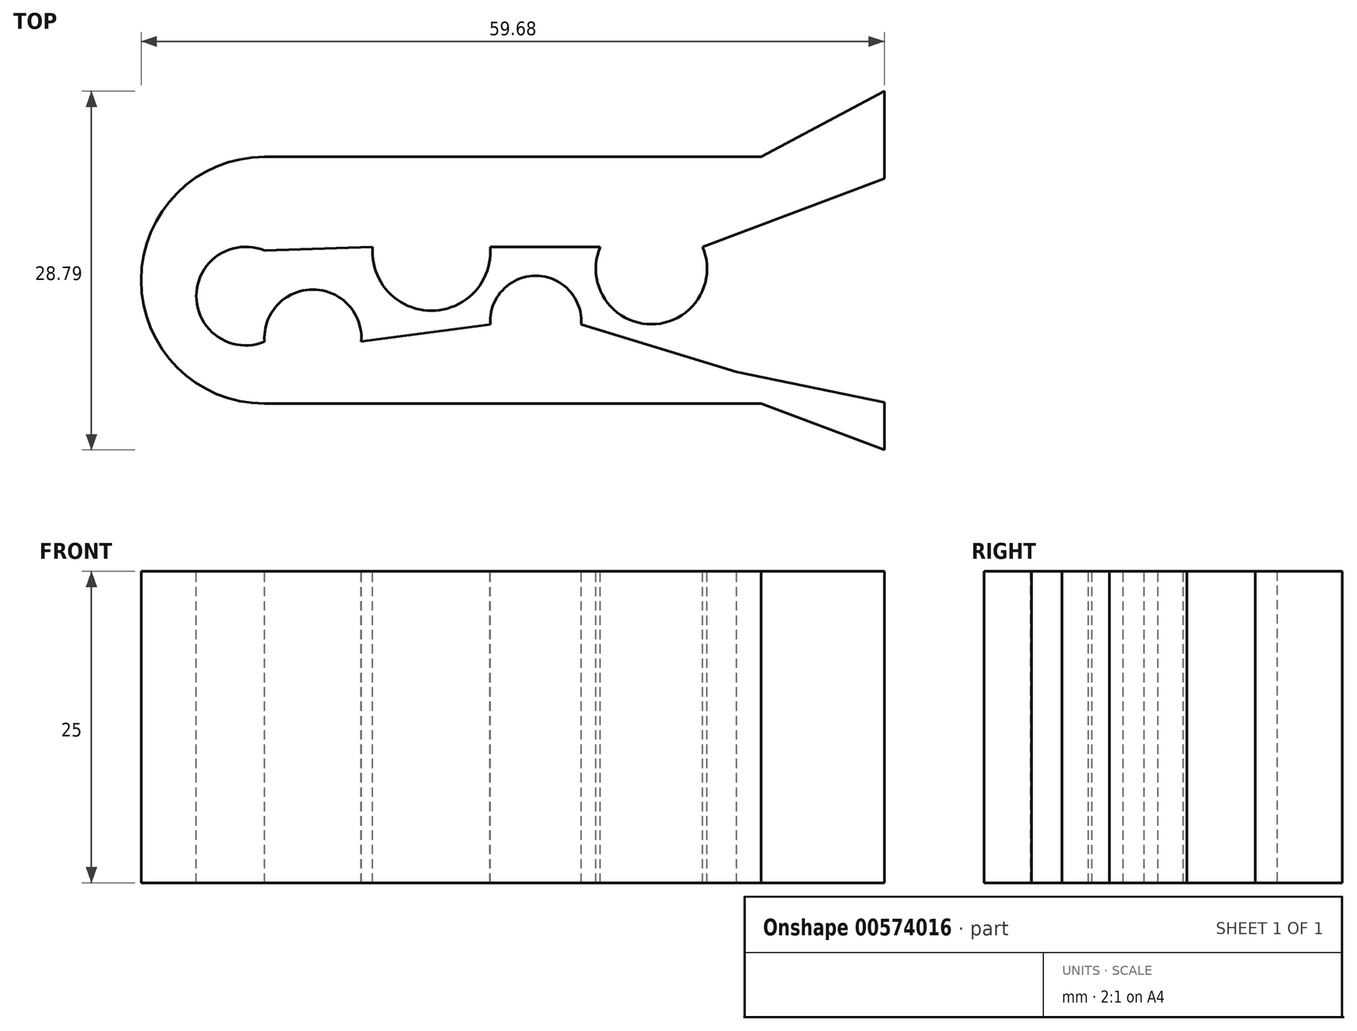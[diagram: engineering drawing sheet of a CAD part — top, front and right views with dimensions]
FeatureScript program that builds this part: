
annotation { "Feature Type Name" : "Feature", "Feature Type Description" : "" }
export const myFeature = defineFeature(function(context is Context, id is Id, definition is map)
    precondition{}
    {
        {
            var Q0;
            Q0=qCreatedBy(makeId("Top.planeOp"),FACE);
            var sketch = newSketch(context, id + "F0", { "sketchPlane" : qUnion([Q0])});
            skLineSegment(sketch, "E0", {"start": v(0, -45.03) * mm, "end": v(39.88, -45.03) * mm});
            skLineSegment(sketch, "E1", {"start": v(39.88, -45.03) * mm, "end": v(49.78, -48.75) * mm});
            skLineSegment(sketch, "E2", {"start": v(49.78, -48.75) * mm, "end": v(49.78, -19.96) * mm});
            skLineSegment(sketch, "E3", {"start": v(49.78, -19.96) * mm, "end": v(39.88, -25.23) * mm});
            skLineSegment(sketch, "E4", {"start": v(39.88, -25.23) * mm, "end": v(0, -25.23) * mm});
            skArc(sketch, "E5", {"start": v(0, -25.23) * mm, "mid": v(-9.9, -35.13) * mm, "end": v(0, -45.03) * mm});
            skSolve(sketch);
        }
        {
            var Q0;
            Q0=makeQuery(id+"F0.imprint","IMPRINT",FACE,{"disambiguationData":[TD([[makeQuery(id+"F0.imprint","IMPRINT",EDGE,{"derivedFrom":sQuery(id+"F0.wireOp",EDGE,"E0")}),1.0]])]});
            extrude(context, id + "F1", {"entities" : qUnion([Q0]), "depth" : 25 * mm, "offsetDistance" : 25 * mm});
        }
        {
            var Q0;
            Q0=makeQuery(id+"F1.opExtrude","CAP_FACE",FACE,{"disambiguationData":[OSD([sQuery(id+"F0.wireOp",EDGE,"E0"),sQuery(id+"F0.wireOp",EDGE,"E1"),sQuery(id+"F0.wireOp",EDGE,"E2"),sQuery(id+"F0.wireOp",EDGE,"E3"),sQuery(id+"F0.wireOp",EDGE,"E4"),sQuery(id+"F0.wireOp",EDGE,"E5")])],"isStart":false});
            var sketch = newSketch(context, id + "F2", { "sketchPlane" : qUnion([Q0])});
            skLineSegment(sketch, "E6", {"start": v(0, -32.44) * mm, "end": v(8.68, -32.44) * mm});
            skArc(sketch, "E7", {"start": v(8.68, -32.44) * mm, "mid": v(13.86, -37.73) * mm, "end": v(19.04, -32.44) * mm});
            skArc(sketch, "E8", {"start": v(0, -32.44) * mm, "mid": v(-6.42, -36.4) * mm, "end": v(0, -40.37) * mm});
            skArc(sketch, "E9", {"start": v(8.68, -40.37) * mm, "mid": v(4.34, -36.28) * mm, "end": v(0, -40.37) * mm});
            skSolve(sketch);
        }
        {
            var Q0;
            Q0=makeQuery(id+"F2.imprint","IMPRINT",FACE,{"disambiguationData":[TD([[makeQuery(id+"F2.imprint","IMPRINT",EDGE,{"derivedFrom":makeQuery(id+"F1.opExtrude","CAP_EDGE",EDGE,{"disambiguationData":[OSD([sQuery(id+"F0.wireOp",EDGE,"E0")])],"isStart":false})}),1.0]])]});
            var sketch = newSketch(context, id + "F3", { "sketchPlane" : qUnion([Q0])});
            skArc(sketch, "E10", {"start": v(0, -32.75) * mm, "mid": v(-5.47, -36.4) * mm, "end": v(0, -40.06) * mm});
            skArc(sketch, "E11", {"start": v(7.77, -40.06) * mm, "mid": v(3.88, -35.87) * mm, "end": v(0, -40.06) * mm});
            skArc(sketch, "E12", {"start": v(8.68, -32.44) * mm, "mid": v(13.4, -37.57) * mm, "end": v(18.13, -32.44) * mm});
            skArc(sketch, "E13", {"start": v(26.96, -32.44) * mm, "mid": v(31.07, -38.67) * mm, "end": v(35.19, -32.44) * mm});
            skArc(sketch, "E14", {"start": v(25.44, -38.67) * mm, "mid": v(21.78, -34.78) * mm, "end": v(18.13, -38.67) * mm});
            skPoint(sketch, "E14.startSnap0", {"position": v(31.07, -38.67) * mm});
            skPoint(sketch, "E14.endSnap0", {"position": v(31.07, -38.67) * mm});
            skLineSegment(sketch, "E15", {"start": v(0, -32.75) * mm, "end": v(8.68, -32.44) * mm});
            skLineSegment(sketch, "E16", {"start": v(18.13, -32.44) * mm, "end": v(26.96, -32.44) * mm});
            skLineSegment(sketch, "E17", {"start": v(7.77, -40.06) * mm, "end": v(18.13, -38.67) * mm});
            skLineSegment(sketch, "E18", {"start": v(25.44, -38.67) * mm, "end": v(37.93, -42.5) * mm});
            skLineSegment(sketch, "E19", {"start": v(37.93, -42.5) * mm, "end": v(49.8, -44.93) * mm});
            skLineSegment(sketch, "E20", {"start": v(49.8, -44.93) * mm, "end": v(49.8, -26.96) * mm});
            skLineSegment(sketch, "E21", {"start": v(49.8, -26.96) * mm, "end": v(35.19, -32.44) * mm});
            skSolve(sketch);
        }
        {
            var Q0;
            Q0=makeQuery(id+"F2.imprint","IMPRINT",FACE,{"disambiguationData":[TD([[makeQuery(id+"F2.imprint","IMPRINT",EDGE,{"derivedFrom":makeQuery(id+"F1.opExtrude","CAP_EDGE",EDGE,{"disambiguationData":[OSD([sQuery(id+"F0.wireOp",EDGE,"E0")])],"isStart":false})}),1.0]])]});
            extrude(context, id + "F4", {"entities" : qUnion([Q0]), "operationType" : NewBodyOperationType.ADD, "oppositeDirection" : true, "depth" : 25 * mm, "offsetDistance" : 25 * mm});
        }
        {
            var Q0;
            Q0=makeQuery(id+"F3.imprint","IMPRINT",FACE,{"disambiguationData":[TD([[makeQuery(id+"F3.imprint","IMPRINT",EDGE,{"derivedFrom":sQuery(id+"F3.wireOp",EDGE,"E10")}),1.0]])]});
            extrude(context, id + "F5", {"entities" : qUnion([Q0]), "operationType" : NewBodyOperationType.REMOVE, "oppositeDirection" : true, "depth" : 25 * mm, "offsetDistance" : 25 * mm});
        }
    });
